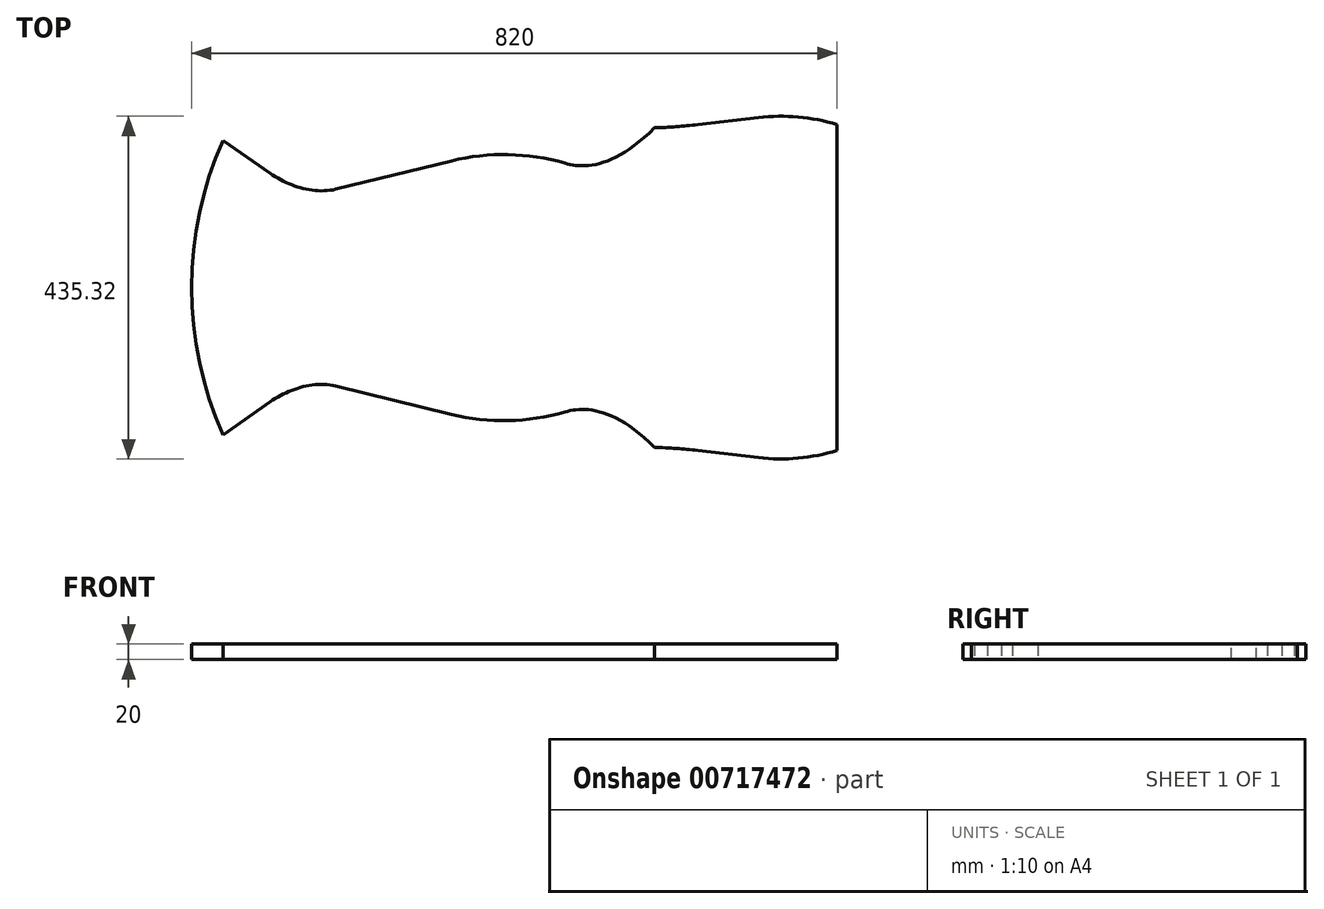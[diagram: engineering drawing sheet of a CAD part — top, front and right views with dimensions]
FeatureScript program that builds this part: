
annotation { "Feature Type Name" : "Feature", "Feature Type Description" : "" }
export const myFeature = defineFeature(function(context is Context, id is Id, definition is map)
    precondition{}
    {
        {
            var Q0;
            Q0=qCreatedBy(makeId("Top.planeOp"),FACE);
            var sketch = newSketch(context, id + "F0", { "sketchPlane" : qUnion([Q0])});
            skLineSegment(sketch, "E0", {"start": v(0, 0) * mm, "end": v(820, 0) * mm});
            skLineSegment(sketch, "E1", {"start": v(100, 0) * mm, "end": v(100, 145) * mm});
            skLineSegment(sketch, "E2", {"start": v(183, 0) * mm, "end": v(183, 125) * mm});
            skLineSegment(sketch, "E3", {"start": v(330, 0) * mm, "end": v(330, 161) * mm});
            skLineSegment(sketch, "E4", {"start": v(474, 0) * mm, "end": v(474, 158) * mm});
            skLineSegment(sketch, "E5", {"start": v(820, 0) * mm, "end": v(820, 207) * mm});
            skLineSegment(sketch, "E6", {"start": v(100, 145) * mm, "end": v(40, 187) * mm});
            skArc(sketch, "E7", {"start": v(0, 0) * mm, "mid": v(10.11, 95.62) * mm, "end": v(40, 187) * mm});
            skLineSegment(sketch, "E8", {"start": v(183, 125) * mm, "end": v(330, 161) * mm});
            skLineSegment(sketch, "E9", {"start": v(643, 207) * mm, "end": v(720, 216) * mm});
            skLineSegment(sketch, "E10", {"start": v(588, 0) * mm, "end": v(588, 203) * mm});
            skArc(sketch, "E11", {"start": v(720, 216) * mm, "mid": v(770.47, 216.67) * mm, "end": v(820, 207) * mm});
            skLineSegment(sketch, "E12", {"start": v(720, 216) * mm, "end": v(720, 0) * mm});
            skArc(sketch, "E13", {"start": v(643, 207) * mm, "mid": v(615.54, 204.4) * mm, "end": v(588, 203) * mm});
            skLineSegment(sketch, "E14", {"start": v(643, 207) * mm, "end": v(643, 0) * mm});
            skFitSpline(sketch, "E15", {"points": [v(100, 145) * mm, v(183, 125) * mm], "startDerivative": vector(69.94, -48.96) * mm, "endDerivative": vector(82.93, 20.3) * mm});
            skArc(sketch, "E16.trimOffspring", {"start": v(474, 158) * mm, "mid": v(402.2, 168.95) * mm, "end": v(330, 161) * mm});
            skFitSpline(sketch, "E17", {"points": [v(474, 158) * mm, v(588, 203) * mm], "startDerivative": vector(73.01, -21.14) * mm, "endDerivative": vector(155.42, 155.42) * mm});
            skLineSegment(sketch, "E18", {"start": v(588, 203) * mm, "end": v(524.47, 139.47) * mm, "construction": true});
            skFitSpline(sketch, "E19.MirrorCS", {"points": [v(100, -145) * mm, v(183, -125) * mm], "startDerivative": vector(69.94, 48.96) * mm, "endDerivative": vector(82.93, -20.3) * mm});
            skArc(sketch, "E20.MirrorCS", {"start": v(474, -158) * mm, "mid": v(402.2, -168.95) * mm, "end": v(330, -161) * mm});
            skArc(sketch, "E21.MirrorCS", {"start": v(0, 0) * mm, "mid": v(10.11, -95.62) * mm, "end": v(40, -187) * mm});
            skLineSegment(sketch, "E22.MirrorCS", {"start": v(720, -216) * mm, "end": v(720, 0) * mm});
            skLineSegment(sketch, "E23.MirrorCS", {"start": v(100, -145) * mm, "end": v(40, -187) * mm});
            skLineSegment(sketch, "E24.MirrorCS", {"start": v(588, 0) * mm, "end": v(588, -203) * mm});
            skLineSegment(sketch, "E25.MirrorCS", {"start": v(183, 0) * mm, "end": v(183, -125) * mm});
            skLineSegment(sketch, "E26.MirrorCS", {"start": v(474, 0) * mm, "end": v(474, -158) * mm});
            skLineSegment(sketch, "E27.MirrorCS", {"start": v(643, -207) * mm, "end": v(720, -216) * mm});
            skLineSegment(sketch, "E28.MirrorCS", {"start": v(330, 0) * mm, "end": v(330, -161) * mm});
            skLineSegment(sketch, "E29.MirrorCS", {"start": v(643, -207) * mm, "end": v(643, 0) * mm});
            skLineSegment(sketch, "E30.MirrorCS", {"start": v(820, 0) * mm, "end": v(820, -207) * mm});
            skArc(sketch, "E31.MirrorCS", {"start": v(720, -216) * mm, "mid": v(770.47, -216.67) * mm, "end": v(820, -207) * mm});
            skLineSegment(sketch, "E32.MirrorCS", {"start": v(183, -125) * mm, "end": v(330, -161) * mm});
            skLineSegment(sketch, "E33.MirrorCS", {"start": v(100, 0) * mm, "end": v(100, -145) * mm});
            skLineSegment(sketch, "E34.MirrorCS", {"start": v(588, -203) * mm, "end": v(524.47, -139.47) * mm, "construction": true});
            skArc(sketch, "E35.MirrorCS", {"start": v(643, -207) * mm, "mid": v(615.54, -204.4) * mm, "end": v(588, -203) * mm});
            skFitSpline(sketch, "E36.MirrorCS", {"points": [v(474, -158) * mm, v(588, -203) * mm], "startDerivative": vector(73.01, 21.14) * mm, "endDerivative": vector(155.42, -155.42) * mm});
            skSolve(sketch);
        }
        {
            var Q0;
            Q0 = qSketchRegion(id + "F0", true);
            extrude(context, id + "F1", {"entities" : qUnion([Q0]), "depth" : 20 * mm, "offsetDistance" : 25 * mm});
        }
    });
